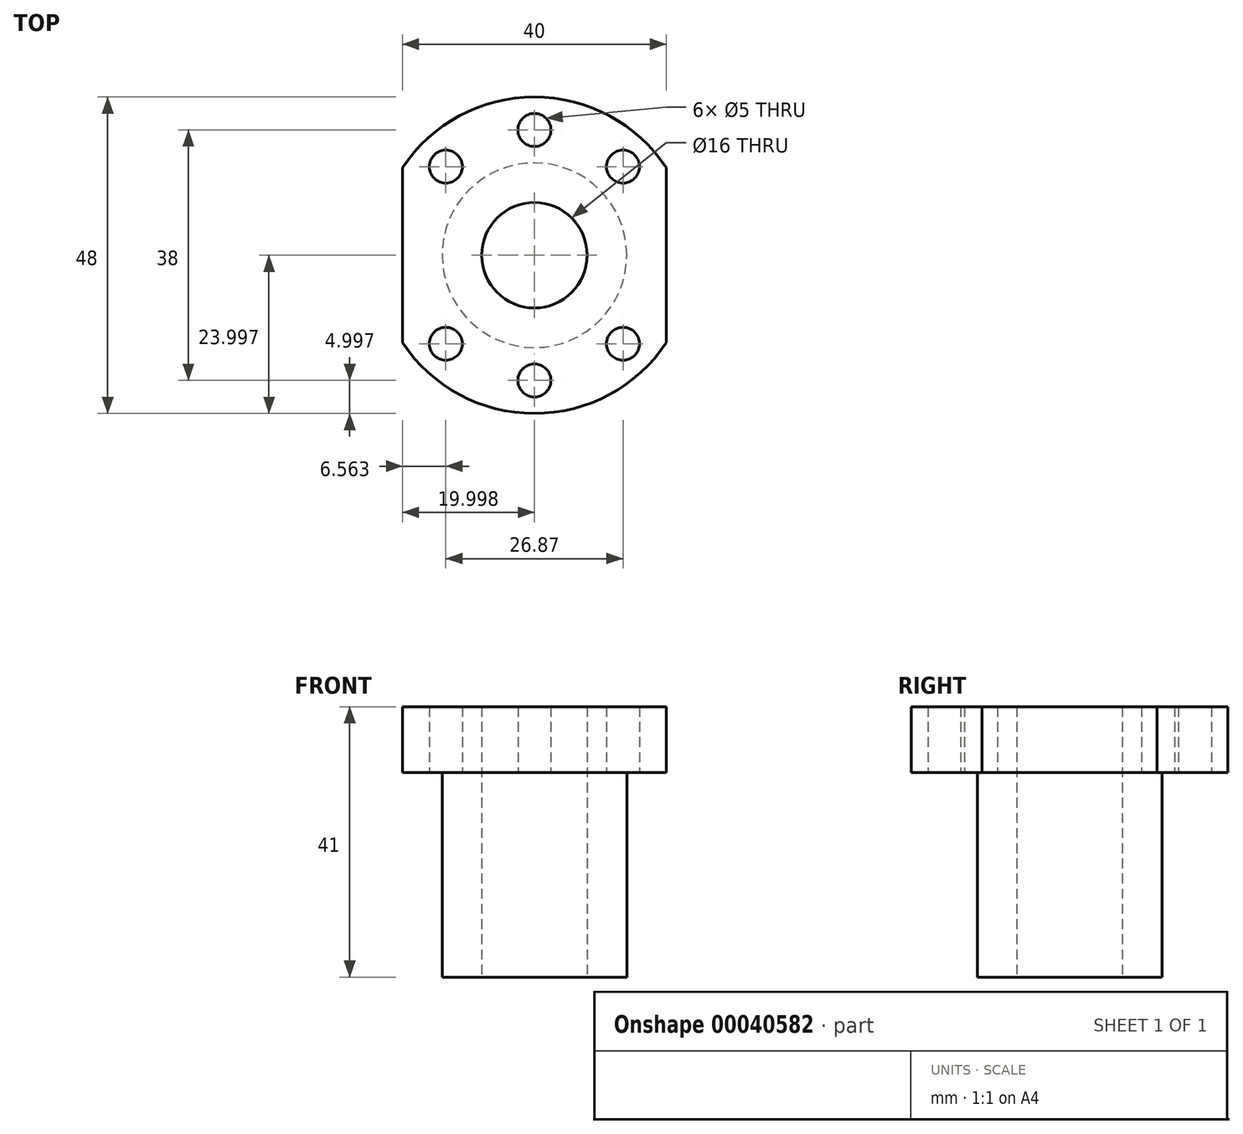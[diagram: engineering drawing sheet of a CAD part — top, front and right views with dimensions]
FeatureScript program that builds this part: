
annotation { "Feature Type Name" : "Feature", "Feature Type Description" : "" }
export const myFeature = defineFeature(function(context is Context, id is Id, definition is map)
    precondition{}
    {
        {
            var Q0;
            Q0=qCreatedBy(makeId("Top.planeOp"),FACE);
            var sketch = newSketch(context, id + "F0", { "sketchPlane" : qUnion([Q0])});
            skCircle(sketch, "E0", {"center": v(-24.74, 7.85) * mm, "radius": 14 * mm});
            skCircle(sketch, "E1", {"center": v(-24.74, 7.85) * mm, "radius": 8 * mm});
            skSolve(sketch);
        }
        {
            var Q0;
            Q0=makeQuery(id+"F0.imprint","IMPRINT",FACE,{"disambiguationData":[TD([[makeQuery(id+"F0.imprint","IMPRINT",EDGE,{"derivedFrom":sQuery(id+"F0.wireOp",EDGE,"E0")}),1.0]])]});
            extrude(context, id + "F1", {"entities" : qUnion([Q0]), "depth" : 31 * mm});
        }
        {
            var Q0;
            Q0=makeQuery(id+"F1.opExtrude","CAP_FACE",FACE,{"disambiguationData":[OSD([sQuery(id+"F0.wireOp",EDGE,"E0"),sQuery(id+"F0.wireOp",EDGE,"E1")])],"isStart":false});
            var sketch = newSketch(context, id + "F2", { "sketchPlane" : qUnion([Q0])});
            skCircle(sketch, "E2", {"center": v(-24.74, 7.85) * mm, "radius": 24 * mm});
            skLineSegment(sketch, "E3", {"start": v(-24.74, -25.69) * mm, "end": v(-24.74, 40.57) * mm, "construction": true});
            skLineSegment(sketch, "E4", {"start": v(-4.74, 35.5) * mm, "end": v(-4.74, -21.48) * mm});
            skLineSegment(sketch, "E5", {"start": v(-44.74, 34.03) * mm, "end": v(-44.74, -23.25) * mm});
            skSolve(sketch);
        }
        {
            var Q0;
            Q0=makeQuery(id+"F2.imprint","IMPRINT",FACE,{"disambiguationData":[TD([[makeQuery(id+"F2.imprint","IMPRINT",EDGE,{"derivedFrom":makeQuery(id+"F1.opExtrude","CAP_EDGE",EDGE,{"disambiguationData":[OSD([sQuery(id+"F0.wireOp",EDGE,"E0")])],"isStart":false})}),-1.0]])]});
            var Q1;
            Q1=makeQuery(id+"F2.imprint","IMPRINT",FACE,{"disambiguationData":[TD([[makeQuery(id+"F2.imprint","IMPRINT",EDGE,{"derivedFrom":makeQuery(id+"F1.opExtrude","CAP_EDGE",EDGE,{"disambiguationData":[OSD([sQuery(id+"F0.wireOp",EDGE,"E0")])],"isStart":false})}),1.0]])]});
            extrude(context, id + "F3", {"entities" : qUnion([Q0, Q1]), "operationType" : NewBodyOperationType.ADD, "depth" : 10 * mm});
        }
        {
            var Q0;
            Q0=makeQuery(id+"F3.opExtrude","CAP_FACE",FACE,{"disambiguationData":[OSD([sQuery(id+"F0.wireOp",EDGE,"E1"),sQuery(id+"F2.wireOp",EDGE,"E2"),sQuery(id+"F2.wireOp",EDGE,"E4"),sQuery(id+"F2.wireOp",EDGE,"E5")])],"isStart":false});
            var sketch = newSketch(context, id + "F4", { "sketchPlane" : qUnion([Q0])});
            skCircle(sketch, "E6", {"center": v(-24.74, 7.85) * mm, "radius": 19 * mm, "construction": true});
            skLineSegment(sketch, "E7", {"start": v(-24.74, 7.85) * mm, "end": v(-24.74, 42.7) * mm, "construction": true});
            skLineSegment(sketch, "E8", {"start": v(-24.74, 7.85) * mm, "end": v(-0.28, 32.3) * mm, "construction": true});
            skLineSegment(sketch, "E9", {"start": v(-24.74, 7.85) * mm, "end": v(-47.36, 30.47) * mm, "construction": true});
            skLineSegment(sketch, "E10", {"start": v(-24.74, 7.85) * mm, "end": v(-24.74, -25.07) * mm, "construction": true});
            skPoint(sketch, "E10.endSnap0", {"position": v(-24.74, -16.15) * mm});
            skLineSegment(sketch, "E11", {"start": v(-24.74, 7.85) * mm, "end": v(-48.96, -16.38) * mm, "construction": true});
            skLineSegment(sketch, "E12", {"start": v(-24.74, 7.85) * mm, "end": v(0.87, -17.76) * mm, "construction": true});
            skPoint(sketch, "E13", {"position": v(-38.18, 21.28) * mm});
            skPoint(sketch, "E14", {"position": v(-24.74, 26.85) * mm});
            skPoint(sketch, "E15", {"position": v(-11.3, 21.28) * mm});
            skPoint(sketch, "E16", {"position": v(-11.3, -5.59) * mm});
            skPoint(sketch, "E17", {"position": v(-24.74, -11.15) * mm});
            skPoint(sketch, "E18", {"position": v(-38.18, -5.59) * mm});
            skSolve(sketch);
        }
        {
            var Q0;
            Q0=sQuery(id+"F4.wireOp",VERTEX,"E13");
            var Q1;
            Q1=sQuery(id+"F4.wireOp",VERTEX,"E14");
            var Q2;
            Q2=sQuery(id+"F4.wireOp",VERTEX,"E15");
            var Q3;
            Q3=sQuery(id+"F4.wireOp",VERTEX,"E16");
            var Q4;
            Q4=sQuery(id+"F4.wireOp",VERTEX,"E17");
            var Q5;
            Q5=sQuery(id+"F4.wireOp",VERTEX,"E18");
            var Q6;
            Q6=makeQuery(id+"F1.opExtrude","SWEPT_BODY",BODY,{"disambiguationData":[OSD([sQuery(id+"F0.wireOp",EDGE,"E0"),sQuery(id+"F0.wireOp",EDGE,"E1")])]});
            hole(context, id + "F5", {"style" : HoleStyle.SIMPLE, "holeDiameter" : 5 * mm, "endStyle" : HoleEndStyle.THROUGH, "locations" : qUnion([Q0, Q1, Q2, Q3, Q4, Q5]), "scope" : qUnion([Q6])});
        }
    });
